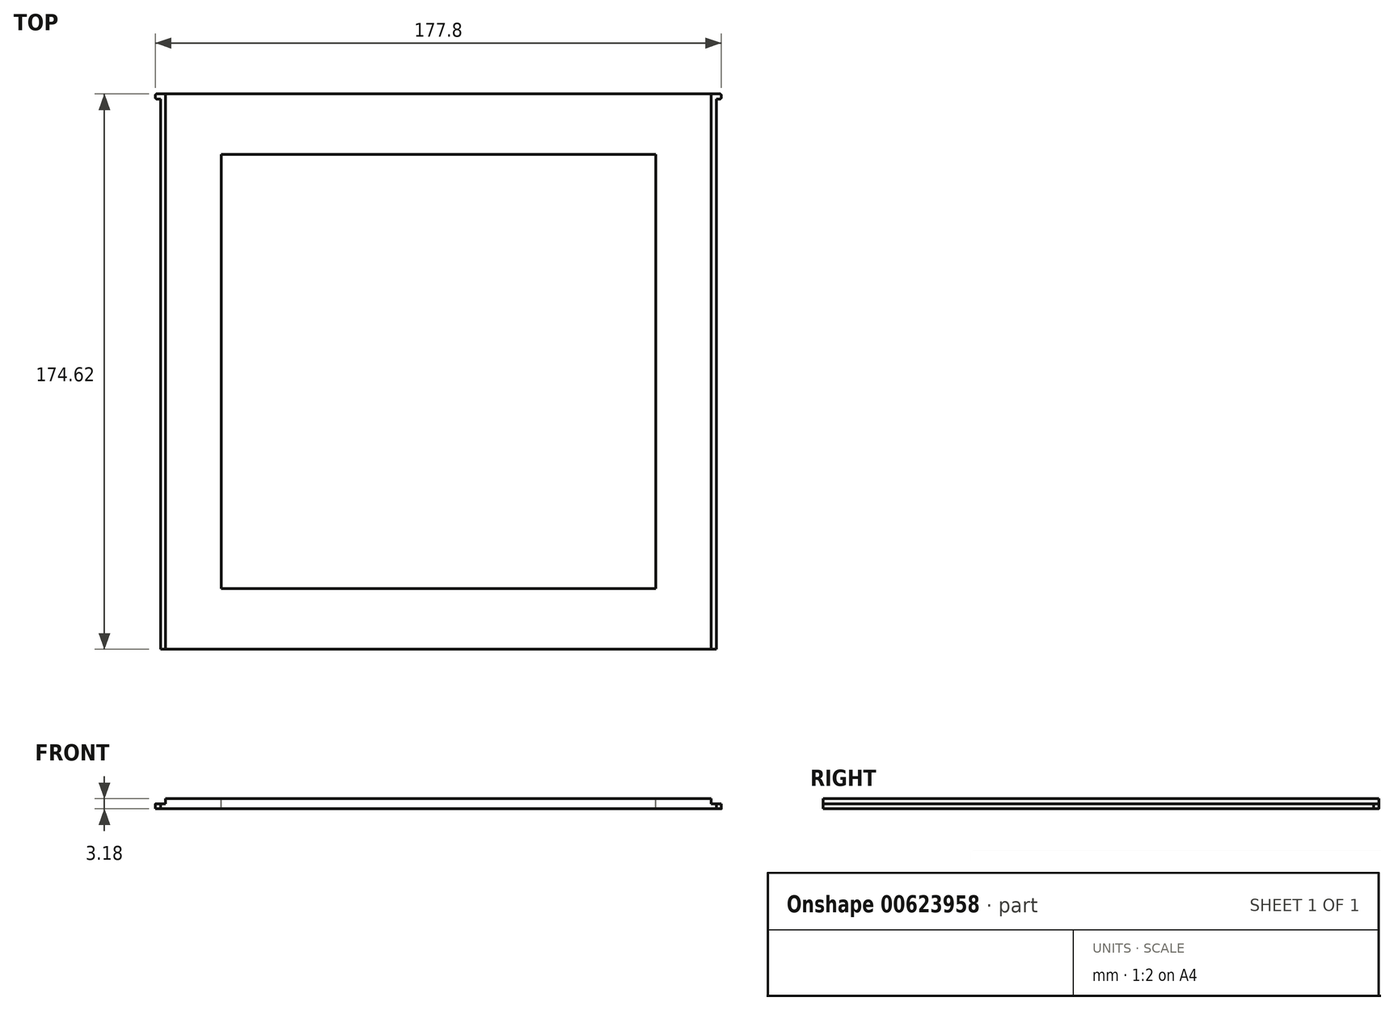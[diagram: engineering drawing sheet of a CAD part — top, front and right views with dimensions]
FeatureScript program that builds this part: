
annotation { "Feature Type Name" : "Feature", "Feature Type Description" : "" }
export const myFeature = defineFeature(function(context is Context, id is Id, definition is map)
    precondition{}
    {
        {
            var Q0;
            Q0=qCreatedBy(makeId("Top.planeOp"),FACE);
            var sketch = newSketch(context, id + "F0", { "sketchPlane" : qUnion([Q0])});
            skLineSegment(sketch, "E0.bottom", {"start": v(-87.31, 88.9) * mm, "end": v(87.31, 88.9) * mm});
            skLineSegment(sketch, "E0.top", {"start": v(-87.31, -85.73) * mm, "end": v(87.31, -85.73) * mm});
            skLineSegment(sketch, "E0.left", {"start": v(-87.31, 87.31) * mm, "end": v(-87.31, -85.73) * mm});
            skLineSegment(sketch, "E0.right", {"start": v(87.31, 87.31) * mm, "end": v(87.31, -85.73) * mm});
            skLineSegment(sketch, "E1.bottom", {"start": v(-87.31, 88.9) * mm, "end": v(-88.52, 88.9) * mm});
            skLineSegment(sketch, "E1.top", {"start": v(-87.31, 87.31) * mm, "end": v(-88.52, 87.31) * mm});
            skLineSegment(sketch, "E1.right", {"start": v(-88.9, 88.52) * mm, "end": v(-88.9, 87.7) * mm});
            skLineSegment(sketch, "E2.bottom", {"start": v(87.31, 88.9) * mm, "end": v(88.52, 88.9) * mm});
            skLineSegment(sketch, "E2.top", {"start": v(87.31, 87.31) * mm, "end": v(88.52, 87.31) * mm});
            skLineSegment(sketch, "E2.right", {"start": v(88.9, 88.52) * mm, "end": v(88.9, 87.7) * mm});
            skPoint(sketch, "E3.visualSharp", {"position": v(-88.9, 87.31) * mm});
            skArc(sketch, "E3.filletArc", {"start": v(-88.9, 87.7) * mm, "mid": v(-88.79, 87.42) * mm, "end": v(-88.52, 87.31) * mm});
            skPoint(sketch, "E4.visualSharp", {"position": v(-88.9, 88.9) * mm});
            skArc(sketch, "E4.filletArc", {"start": v(-88.52, 88.9) * mm, "mid": v(-88.79, 88.79) * mm, "end": v(-88.9, 88.52) * mm});
            skPoint(sketch, "E5.visualSharp", {"position": v(88.9, 88.9) * mm});
            skArc(sketch, "E5.filletArc", {"start": v(88.9, 88.52) * mm, "mid": v(88.79, 88.79) * mm, "end": v(88.52, 88.9) * mm});
            skPoint(sketch, "E6.visualSharp", {"position": v(88.9, 87.31) * mm});
            skArc(sketch, "E6.filletArc", {"start": v(88.52, 87.31) * mm, "mid": v(88.79, 87.42) * mm, "end": v(88.9, 87.7) * mm});
            skSolve(sketch);
        }
        {
            var Q0;
            Q0=qSketchRegion(id+"F0",true);
            extrude(context, id + "F1", {"entities" : qUnion([Q0]), "depth" : 1.59 * mm, "offsetDistance" : 25.4 * mm});
        }
        {
            var Q0;
            Q0=makeQuery(id+"F1.opExtrude","CAP_FACE",FACE,{"disambiguationData":[OSD([sQuery(id+"F0.wireOp",EDGE,"E0.bottom"),sQuery(id+"F0.wireOp",EDGE,"E0.top"),sQuery(id+"F0.wireOp",EDGE,"E0.left"),sQuery(id+"F0.wireOp",EDGE,"E0.right"),sQuery(id+"F0.wireOp",EDGE,"E1.bottom"),sQuery(id+"F0.wireOp",EDGE,"E1.top"),sQuery(id+"F0.wireOp",EDGE,"E1.right"),sQuery(id+"F0.wireOp",EDGE,"E2.bottom"),sQuery(id+"F0.wireOp",EDGE,"E2.top"),sQuery(id+"F0.wireOp",EDGE,"E2.right"),sQuery(id+"F0.wireOp",EDGE,"E3.filletArc"),sQuery(id+"F0.wireOp",EDGE,"E4.filletArc"),sQuery(id+"F0.wireOp",EDGE,"E5.filletArc"),sQuery(id+"F0.wireOp",EDGE,"E6.filletArc")])],"isStart":false});
            var sketch = newSketch(context, id + "F2", { "sketchPlane" : qUnion([Q0])});
            skLineSegment(sketch, "E7.bottom", {"start": v(85.73, -85.73) * mm, "end": v(-85.72, -85.73) * mm});
            skLineSegment(sketch, "E7.top", {"start": v(85.72, 88.9) * mm, "end": v(-85.73, 88.9) * mm});
            skLineSegment(sketch, "E7.left", {"start": v(85.73, -85.73) * mm, "end": v(85.72, 88.9) * mm});
            skLineSegment(sketch, "E7.right", {"start": v(-85.72, -85.73) * mm, "end": v(-85.73, 88.9) * mm});
            skSolve(sketch);
        }
        {
            var Q0;
            Q0=qSketchRegion(id+"F2",true);
            extrude(context, id + "F3", {"entities" : qUnion([Q0]), "operationType" : NewBodyOperationType.ADD, "depth" : 1.59 * mm, "offsetDistance" : 25.4 * mm});
        }
        {
            var Q0;
            Q0=makeQuery(id+"F3.opExtrude","CAP_FACE",FACE,{"disambiguationData":[OSD([sQuery(id+"F2.wireOp",EDGE,"E7.bottom"),sQuery(id+"F2.wireOp",EDGE,"E7.top"),sQuery(id+"F2.wireOp",EDGE,"E7.left"),sQuery(id+"F2.wireOp",EDGE,"E7.right")])],"isStart":false});
            var sketch = newSketch(context, id + "F4", { "sketchPlane" : qUnion([Q0])});
            skLineSegment(sketch, "E8.bottom", {"start": v(-68.26, 69.85) * mm, "end": v(68.26, 69.85) * mm});
            skLineSegment(sketch, "E8.top", {"start": v(-68.26, -66.68) * mm, "end": v(68.26, -66.68) * mm});
            skLineSegment(sketch, "E8.left", {"start": v(-68.26, 69.85) * mm, "end": v(-68.26, -66.68) * mm});
            skLineSegment(sketch, "E8.right", {"start": v(68.26, 69.85) * mm, "end": v(68.26, -66.68) * mm});
            skSolve(sketch);
        }
        {
            var Q0;
            Q0=qSketchRegion(id+"F4",true);
            extrude(context, id + "F5", {"entities" : qUnion([Q0]), "operationType" : NewBodyOperationType.REMOVE, "oppositeDirection" : true, "depth" : 25.4 * mm, "offsetDistance" : 25.4 * mm});
        }
    });
